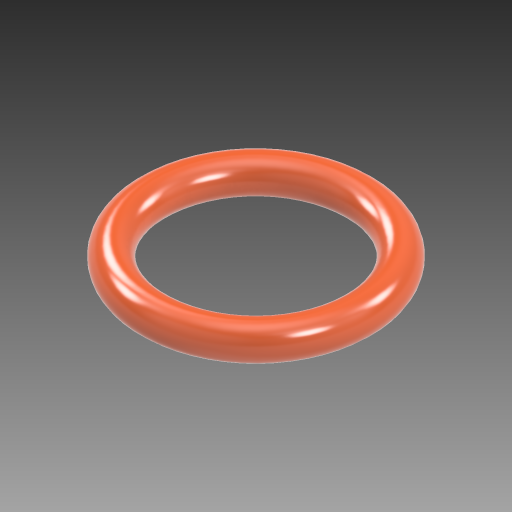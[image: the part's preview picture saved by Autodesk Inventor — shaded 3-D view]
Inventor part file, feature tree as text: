
AUTODESK INVENTOR PART (.ipt)
format: ipt  version: 2024 (Build 280153000, 153)  size: 181,760 bytes
history: native  units: in
note: dims shown in document units (in); Inventor stores cm internally (conversion verified against a paired STEP export)
features: revolve x1, sketch x1
ambient origin geometry x8: Origin, YZ Plane, XZ Plane, XY Plane, X Axis, Y Axis, Z Axis, Center Point
bodies: Solid1 (feature_tree)
feature tree (2):
  revolve  "Revolution1"  [1 undecoded]
  sketch  "Sketch1"  dims[d0=2.0in d1=12.0in d2=90.0deg]
note: 1 required parameter value undecoded (feature->parameter linkage not recoverable at this tier; creation-order binding heuristic only, values carry confidence <= 0.55)
